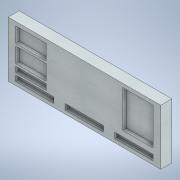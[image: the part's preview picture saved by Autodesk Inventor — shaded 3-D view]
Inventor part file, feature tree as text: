
AUTODESK INVENTOR PART (.ipt)
format: ipt  version: 2022.4 (Build 264492010, 492A)  size: 211,456 bytes
history: native  units: mm
features: extrude x3, sketch x3, other x1
ambient origin geometry x8: Origin, YZ Plane, XZ Plane, XY Plane, X Axis, Y Axis, Z Axis, Center Point
bodies: Body1 (feature_tree)
feature tree (7):
  other  "Sólido1"
  extrude  "Extrusión1"  Depth=137.5mm
  extrude  "Extrusión2"  Depth=27.5mm
  extrude  "Extrusión3"  Depth=20.0mm
  sketch  "Boceto1"  dims[d3=0.0mm d4=137.5mm]
  sketch  "Boceto2"  dims[d5=20.0mm d6=27.5mm]
  sketch  "Boceto3"  dims[d7=137.5mm d8=20.0mm d9=27.5mm d10=13.333333mm d11=13.333333mm d12=137.5mm d13=41.25mm d14=41.25mm d15=20.0mm d17=110.0mm d18=133.333333mm d19=27.5mm d20=13.333333mm d21=110.0mm d22=55.0mm d23=27.5mm d24=13.333333mm d25=110.0mm d26=55.0mm d27=27.5mm d28=7.843137mm d29=110.0mm d30=20.0mm d31=7.843137mm d32=7.647059mm d33=13.333333mm d34=0.0mm d35=20.0mm d36=20.0mm d37=20.0mm d38=20.0mm d39=20.0mm d40=66.666667mm d41=20.0mm d42=66.666667mm d43=20.0mm d44=66.666667mm d45=20.0mm d46=66.666667mm d47=13.333333mm d48=0.0mm]
